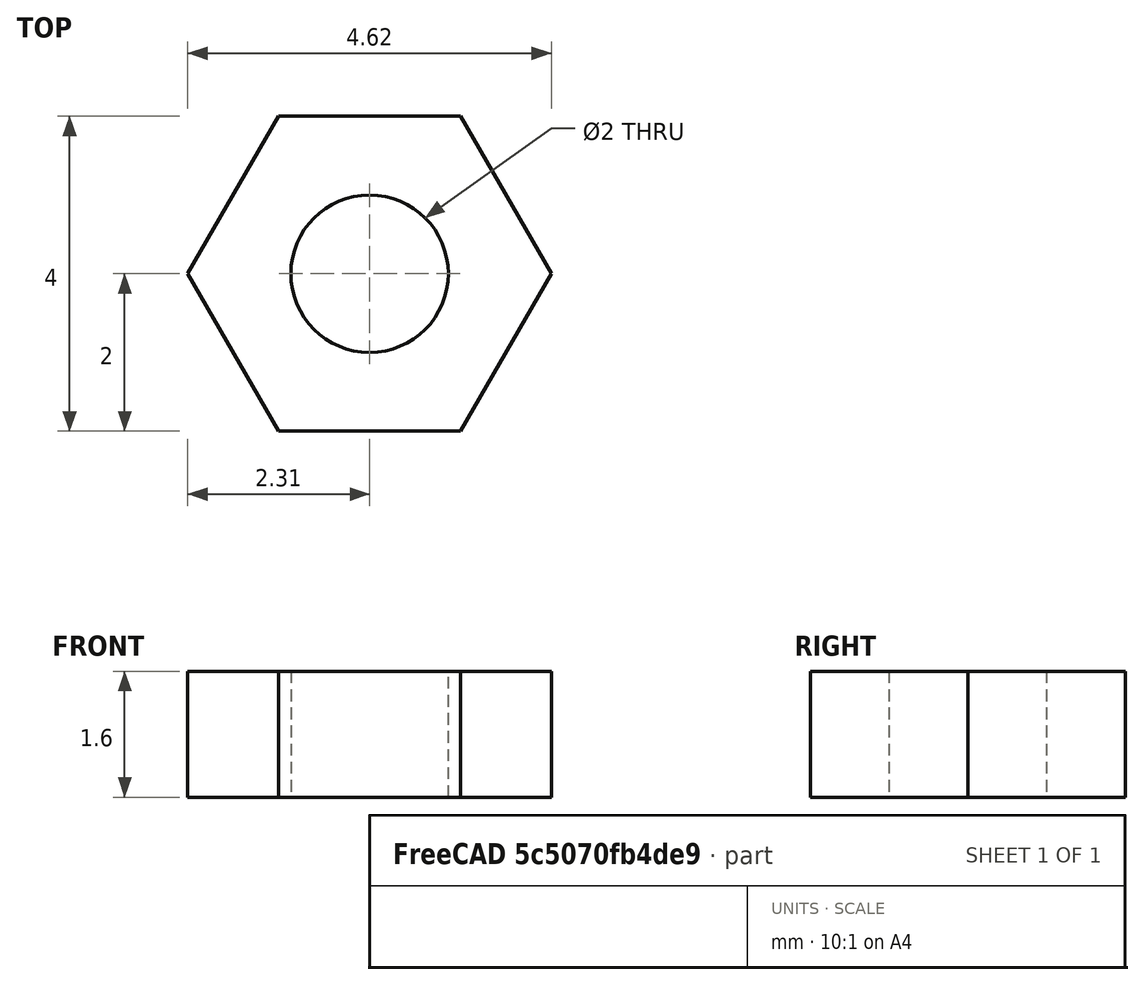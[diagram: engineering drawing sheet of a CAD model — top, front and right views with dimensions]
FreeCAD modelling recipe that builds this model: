
FCSTD DOCUMENT  (FreeCAD 1.0R39319 (Git))
Label: ecrouM2
License: All rights reserved
LicenseURL: https://en.wikipedia.org/wiki/All_rights_reserved
objects: Sketcher::SketchObject×1, PartDesign::Pad×1, PartDesign::Body×1
note: 6 computed .brp shape members not serialized (recipe doc carries the construction recipe); baked Part::Feature solids carry a one-line shape summary decoded from their .brp

FEATURE [Sketcher::SketchObject] Sketch
  ArcFitTolerance = 1e-06
  AttachmentSupport = -> [XY_Plane]
  FullyConstrained = true
  MakeInternals = false
  MapMode = 5
  sketch-geometry (8):
    g0: LineSegment StartX=-1.1547 StartY=2 StartZ=0 EndX=-2.3094 EndY=3.42e-14 EndZ=0
    g1: LineSegment StartX=-2.3094 StartY=3.42e-14 StartZ=0 EndX=-1.1547 EndY=-2 EndZ=0
    g2: LineSegment StartX=-1.1547 StartY=-2 StartZ=0 EndX=1.1547 EndY=-2 EndZ=0
    g3: LineSegment StartX=1.1547 StartY=-2 StartZ=0 EndX=2.3094 EndY=0 EndZ=0
    g4: LineSegment StartX=2.3094 StartY=0 StartZ=0 EndX=1.1547 EndY=2 EndZ=0
    g5: LineSegment StartX=1.1547 StartY=2 StartZ=0 EndX=-1.1547 EndY=2 EndZ=0
    g6: Circle [constr] CenterX=0 CenterY=0 CenterZ=0 NormalX=0 NormalY=0 NormalZ=1 AngleXU=0 Radius=2.3094
    g7: Circle CenterX=0 CenterY=0 CenterZ=0 NormalX=0 NormalY=0 NormalZ=1 AngleXU=0 Radius=1
  constraints (18):
    c: Coincident(g0,g1)
    c: Coincident(g1,g2)
    c: Coincident(g2,g3)
    c: Coincident(g3,g4)
    c: Coincident(g4,g5)
    c: Coincident(g5,g0)
    c: Equal(g0, g1-g5) x5
    c: PointOnObject(g0,g6)
    c: PointOnObject(g1,g6)
    c: PointOnObject(g2,g6)
    c: PointOnObject(g3,g6)
    c: PointOnObject(g4,g6)
    c: PointOnObject(g5,g6)
    c: Coincident(g6,g-1)
    c: PointOnObject(g3,g-1)
    c: Distance(g1,g4) = 4
    c: Coincident(g7,g6)
    c: Diameter(g7) = 2
FEATURE [PartDesign::Pad] Pad
  Direction = (0,0,1)
  Length = 1.6
  Length2 = 10
  Profile = -> Sketch
  ReferenceAxis = -> Sketch [N_Axis]
  Refine = true
  Suppressed = false
  Type = 0
FEATURE [PartDesign::Body] Body  label="Corps"
  AllowCompound = false
  Group = -> [Sketch,Pad]
  Origin = -> Origin
  Tip = -> Pad
